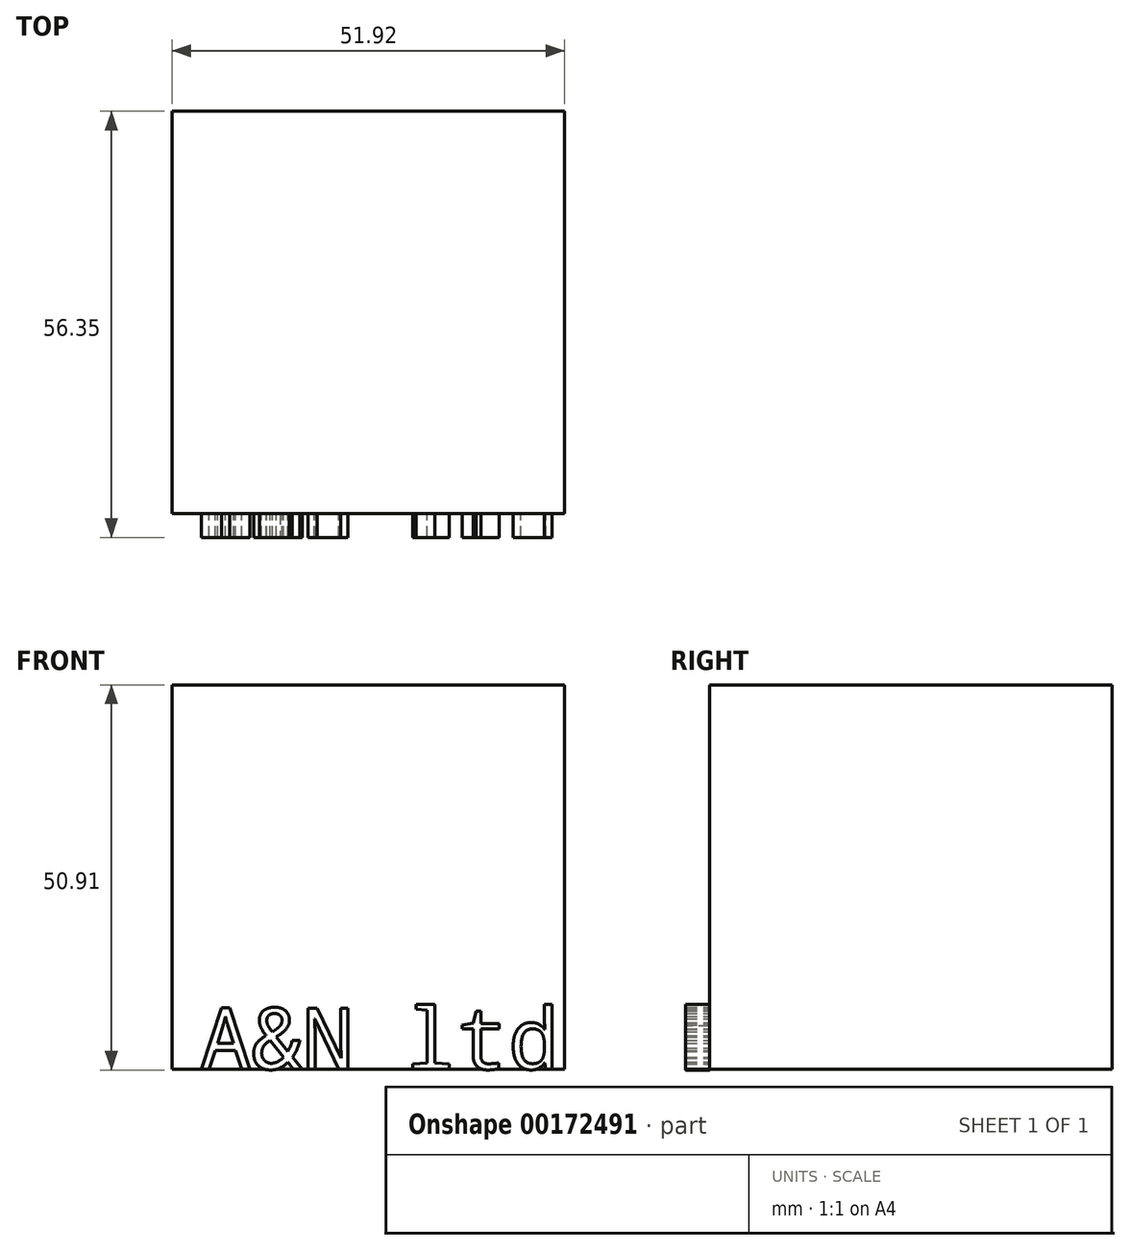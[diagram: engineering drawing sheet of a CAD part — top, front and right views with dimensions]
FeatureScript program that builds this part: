
annotation { "Feature Type Name" : "Feature", "Feature Type Description" : "" }
export const myFeature = defineFeature(function(context is Context, id is Id, definition is map)
    precondition{}
    {
        {
            var Q0;
            Q0=qCreatedBy(makeId("Top.planeOp"),FACE);
            var sketch = newSketch(context, id + "F0", { "sketchPlane" : qUnion([Q0])});
            skLineSegment(sketch, "E0.bottom", {"start": v(-25.96, 26.59) * mm, "end": v(25.96, 26.59) * mm});
            skLineSegment(sketch, "E0.top", {"start": v(-25.96, -26.59) * mm, "end": v(25.96, -26.59) * mm});
            skLineSegment(sketch, "E0.left", {"start": v(-25.96, 26.59) * mm, "end": v(-25.96, -26.59) * mm});
            skLineSegment(sketch, "E0.right", {"start": v(25.96, 26.59) * mm, "end": v(25.96, -26.59) * mm});
            skPoint(sketch, "E0.middle", {"position": v(0, 0) * mm});
            skSolve(sketch);
        }
        {
            var Q0;
            Q0 = qSketchRegion(id + "F0", true);
            extrude(context, id + "F1", {"entities" : qUnion([Q0]), "depth" : 50.8 * mm});
        }
        {
            var Q0;
            Q0=makeQuery(id+"F1.opExtrude","SWEPT_FACE",FACE,{"disambiguationData":[OSD([sQuery(id+"F0.wireOp",EDGE,"E0.top")])]});
            var sketch = newSketch(context, id + "F2", { "sketchPlane" : qUnion([Q0])});
            skText(sketch, "E1", { "text": "A&N ltd", "fontName": "DroidSansMono.ttf"});
            const initialGuessF2  = {"E1": [-0.02227, 0, 1, 0, 0.00813]};
            skSetInitialGuess(sketch, initialGuessF2);
            skSolve(sketch);
        }
        {
            var Q0;
            Q0 = qSketchRegion(id + "F2", true);
            extrude(context, id + "F3", {"entities" : qUnion([Q0]), "operationType" : NewBodyOperationType.ADD, "depth" : 3.17 * mm});
        }
    });
